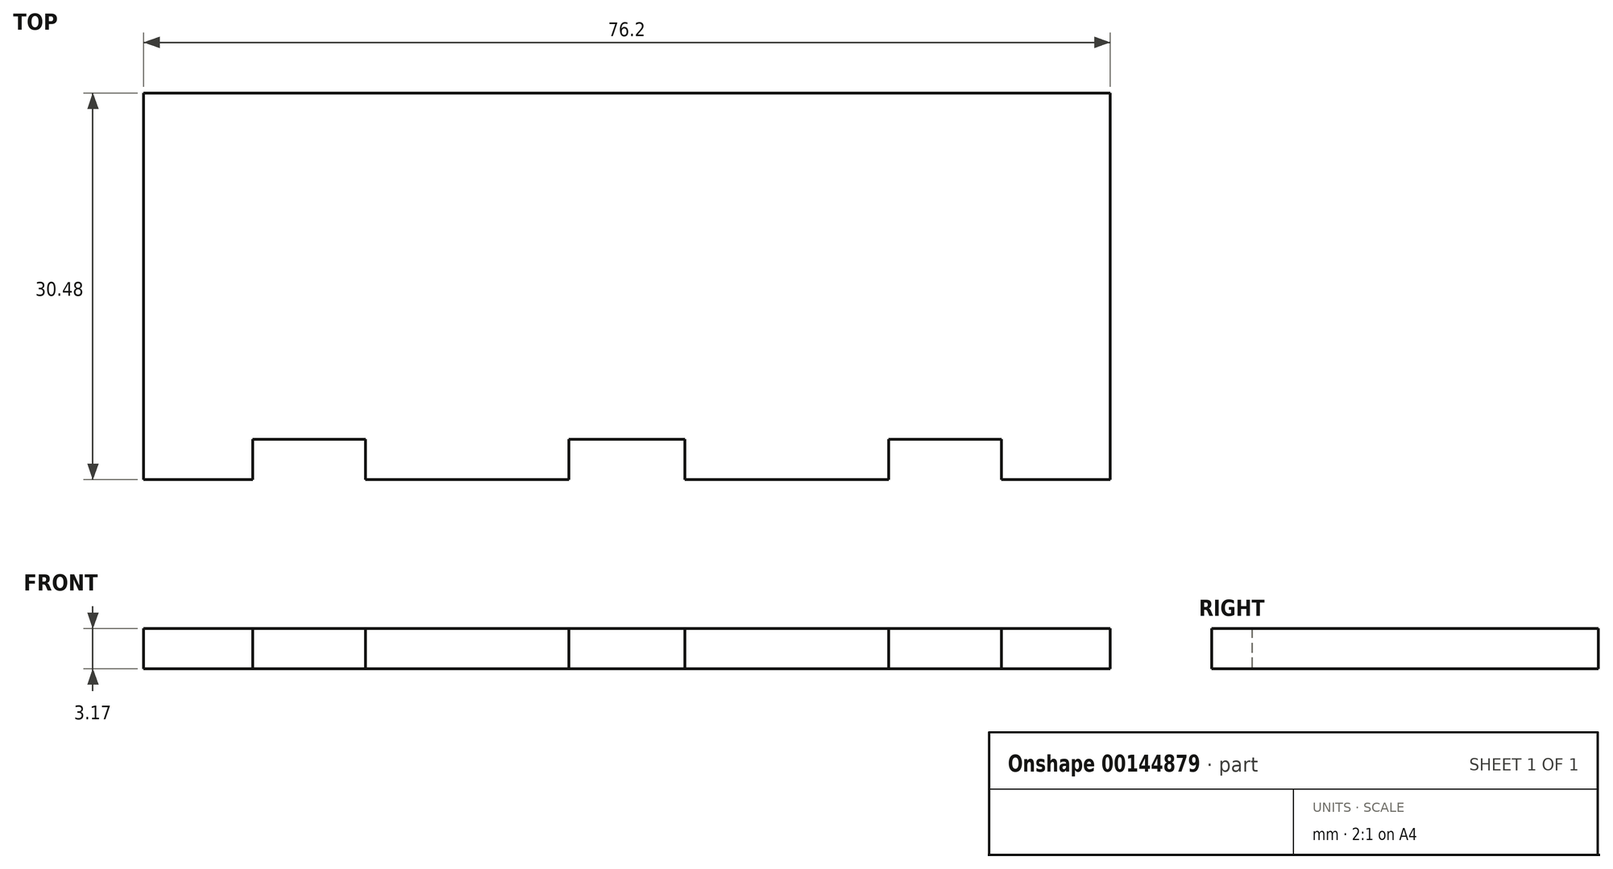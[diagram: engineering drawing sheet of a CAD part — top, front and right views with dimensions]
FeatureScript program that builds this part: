
annotation { "Feature Type Name" : "Feature", "Feature Type Description" : "" }
export const myFeature = defineFeature(function(context is Context, id is Id, definition is map)
    precondition{}
    {
        {
            var Q0;
            Q0=qCreatedBy(makeId("Top.planeOp"),FACE);
            var sketch = newSketch(context, id + "F0", { "sketchPlane" : qUnion([Q0])});
            skLineSegment(sketch, "E0.bottom", {"start": v(-38.1, 15.24) * mm, "end": v(38.1, 15.24) * mm});
            skLineSegment(sketch, "E0.top", {"start": v(-38.1, -15.24) * mm, "end": v(38.1, -15.24) * mm});
            skLineSegment(sketch, "E0.left", {"start": v(-38.1, 15.24) * mm, "end": v(-38.1, -15.24) * mm});
            skLineSegment(sketch, "E0.right", {"start": v(38.1, 15.24) * mm, "end": v(38.1, -15.24) * mm});
            skPoint(sketch, "E0.middle", {"position": v(0, 0) * mm});
            skLineSegment(sketch, "E1.bottom", {"start": v(-29.51, 15.24) * mm, "end": v(-20.62, 15.24) * mm});
            skLineSegment(sketch, "E2.bottom", {"start": v(29.51, 15.24) * mm, "end": v(20.62, 15.24) * mm});
            skLineSegment(sketch, "E3.top", {"start": v(-29.51, 18.42) * mm, "end": v(-20.62, 18.42) * mm});
            skLineSegment(sketch, "E3.left", {"start": v(-29.51, 15.24) * mm, "end": v(-29.51, 18.42) * mm});
            skLineSegment(sketch, "E3.right", {"start": v(-20.62, 15.24) * mm, "end": v(-20.62, 18.41) * mm});
            skLineSegment(sketch, "E4.top", {"start": v(20.62, 18.42) * mm, "end": v(29.51, 18.42) * mm});
            skLineSegment(sketch, "E4.left", {"start": v(20.62, 15.24) * mm, "end": v(20.62, 18.42) * mm});
            skLineSegment(sketch, "E4.right", {"start": v(29.51, 15.24) * mm, "end": v(29.51, 18.42) * mm});
            skPoint(sketch, "E5", {"position": v(0, 15.24) * mm});
            skPoint(sketch, "E6", {"position": v(-4.57, 15.24) * mm});
            skPoint(sketch, "E7", {"position": v(4.57, 15.24) * mm});
            skLineSegment(sketch, "E8.bottom", {"start": v(-4.57, 15.24) * mm, "end": v(4.57, 15.24) * mm});
            skLineSegment(sketch, "E8.top", {"start": v(-4.57, 18.42) * mm, "end": v(4.57, 18.42) * mm});
            skLineSegment(sketch, "E8.left", {"start": v(-4.57, 15.24) * mm, "end": v(-4.57, 18.42) * mm});
            skLineSegment(sketch, "E8.right", {"start": v(4.57, 15.24) * mm, "end": v(4.57, 18.42) * mm});
            skLineSegment(sketch, "E9.bottom", {"start": v(-29.51, -15.24) * mm, "end": v(-20.62, -15.24) * mm});
            skLineSegment(sketch, "E9.top", {"start": v(-29.51, -12.06) * mm, "end": v(-20.62, -12.06) * mm});
            skLineSegment(sketch, "E9.left", {"start": v(-29.51, -15.24) * mm, "end": v(-29.51, -12.06) * mm});
            skLineSegment(sketch, "E9.right", {"start": v(-20.62, -15.24) * mm, "end": v(-20.62, -12.06) * mm});
            skLineSegment(sketch, "E10.bottom", {"start": v(-4.57, -15.24) * mm, "end": v(4.57, -15.24) * mm});
            skLineSegment(sketch, "E10.top", {"start": v(-4.57, -12.06) * mm, "end": v(4.57, -12.06) * mm});
            skLineSegment(sketch, "E10.left", {"start": v(-4.57, -15.24) * mm, "end": v(-4.57, -12.06) * mm});
            skLineSegment(sketch, "E10.right", {"start": v(4.57, -15.24) * mm, "end": v(4.57, -12.06) * mm});
            skLineSegment(sketch, "E11.bottom", {"start": v(20.62, -15.24) * mm, "end": v(29.51, -15.24) * mm});
            skLineSegment(sketch, "E11.top", {"start": v(20.62, -12.06) * mm, "end": v(29.51, -12.06) * mm});
            skLineSegment(sketch, "E11.left", {"start": v(20.62, -15.24) * mm, "end": v(20.62, -12.06) * mm});
            skLineSegment(sketch, "E11.right", {"start": v(29.51, -15.24) * mm, "end": v(29.51, -12.06) * mm});
            skSolve(sketch);
        }
        {
            var Q0;
            Q0=makeQuery(id+"F0.imprint","IMPRINT",FACE,{"disambiguationData":[TD([[makeQuery(id+"F0.imprint","IMPRINT",EDGE,{"derivedFrom":sQuery(id+"F0.wireOp",EDGE,"E1.bottom")}),1.0]])]});
            var Q1;
            Q1=makeQuery(id+"F0.imprint","IMPRINT",FACE,{"disambiguationData":[TD([[makeQuery(id+"F0.imprint","IMPRINT",EDGE,{"derivedFrom":sQuery(id+"F0.wireOp",EDGE,"E0.top")}),1.0]])]});
            var Q2;
            Q2=makeQuery(id+"F0.imprint","IMPRINT",FACE,{"disambiguationData":[TD([[makeQuery(id+"F0.imprint","IMPRINT",EDGE,{"derivedFrom":sQuery(id+"F0.wireOp",EDGE,"E8.bottom")}),1.0]])]});
            var Q3;
            Q3=makeQuery(id+"F0.imprint","IMPRINT",FACE,{"disambiguationData":[TD([[makeQuery(id+"F0.imprint","IMPRINT",EDGE,{"derivedFrom":sQuery(id+"F0.wireOp",EDGE,"E2.bottom")}),-1.0]])]});
            extrude(context, id + "F1", {"entities" : qUnion([Q0, Q1, Q2, Q3]), "depth" : 3.17 * mm});
        }
    });
